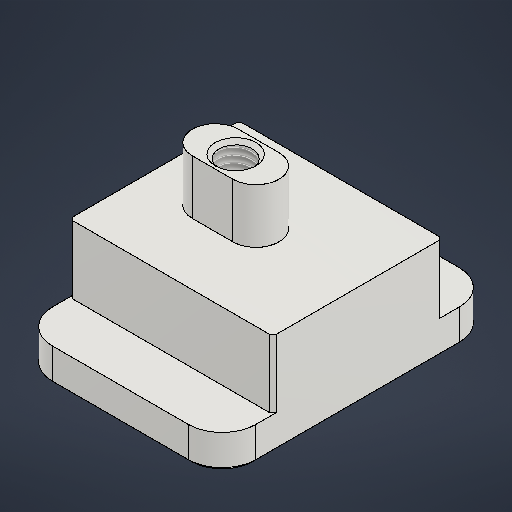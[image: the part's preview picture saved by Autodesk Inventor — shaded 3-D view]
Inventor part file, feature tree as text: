
AUTODESK INVENTOR PART (.ipt)
format: ipt  version: 2025.3 (Build 293356000, 356)  size: 249,856 bytes
history: native  units: mm
features: extrude x4, sketch x2, hole x1, fillet x1, chamfer x1
ambient origin geometry x8: Origin, YZ Plane, XZ Plane, XY Plane, X Axis, Y Axis, Z Axis, Center Point
bodies: Solid1 (feature_tree)
feature tree (9):
  sketch  "Sketch1"  dims[d0=40.0mm d1=30.0mm]
  extrude  "Extrusion1"  Depth=30.0mm
  extrude  "Extrusion2"  Depth=6.8mm
  extrude  "Extrusion5"  Depth=23.0mm
  extrude  "Extrusion6"  TaperAngle=0.0deg  [1 undecoded]
  hole  "Hole1"  [1 undecoded]
  fillet  "Fillet1"  [1 undecoded]
  chamfer  "Chamfer1"  Distance=10.0mm
  sketch  "Sketch3"  dims[d2=6.0mm d3=6.8mm d4=23.0mm d5=0.0mm d6=8.0mm d7=0.0mm d8=4.917mm d9=10.0mm d10=6.0mm d11=2.0mm d12=90.0deg d13=15.0mm d14=0.0mm d15=5.0mm d16=0.5mm d17=2.0mm d18=45.0deg d19=3.0mm d29=15.0mm d30=10.0mm d31=0.0mm d35=25.0mm d36=18.0mm d37=0.0mm]
note: 3 required parameter values undecoded (feature->parameter linkage not recoverable at this tier; creation-order binding heuristic only, values carry confidence <= 0.55)
